# Revit family: UP-EB-Dose 1f Gira E22
name_source: partatom
category: Electrical Fixtures
revit_build: Autodesk Revit 2017 (Build: 20160225_1515(x64)
units: mm (PartAtom-declared; Revit-internal decimal feet)

## family parameters
Cut with Voids When Loaded = No
Host = Face
Maintain Annotation Orientation = No
Part Type = Normal
Room Calculation Point = No
Round Connector Dimension = Use Diameter
Shared = No

## types (1)
- UP-EB-Dose 1f Gira E22
    Available = Yes
    BIM (1) = https://media.live.bim.site
    Category = Ersatzteil für Installationsschalterprogramme
    Data sheet (1) = https://katalog.gira.de
    Default Elevation = 1219 mm
    Description = Unterputz-Einbaudose Gira E2, Gira E22  1fach Merkmale: - Mauerwerkmontage durch Befestigung der Unterputz-Einbaudose, z. B. fixieren mit Gips. Montage der Gerätedose in der Unterputz-Einbaudose wie bei einer marktüblichen Hohlwanddose.
    GTIN = 4010337049784
    HAN = 289100
    HeinzeBIM = https://bimportal.heinze.de
    Kategorie = Ersatzteil für Installationsschalterprogramme
    Keynote = UP-EB-Dose_4fach
    Manufacturer = Gira
    Manufacturer URL = https://www.gira.de
    Name = UP-EB-Dose 1f Gira E22
    Region = DE
    URL = http://katalog.gira.de
    Verfügbar = Ja

## geometry (parser evidence)
native form markers: Blend x2, Sweep x2
no freeform markers — native parametric forms only
